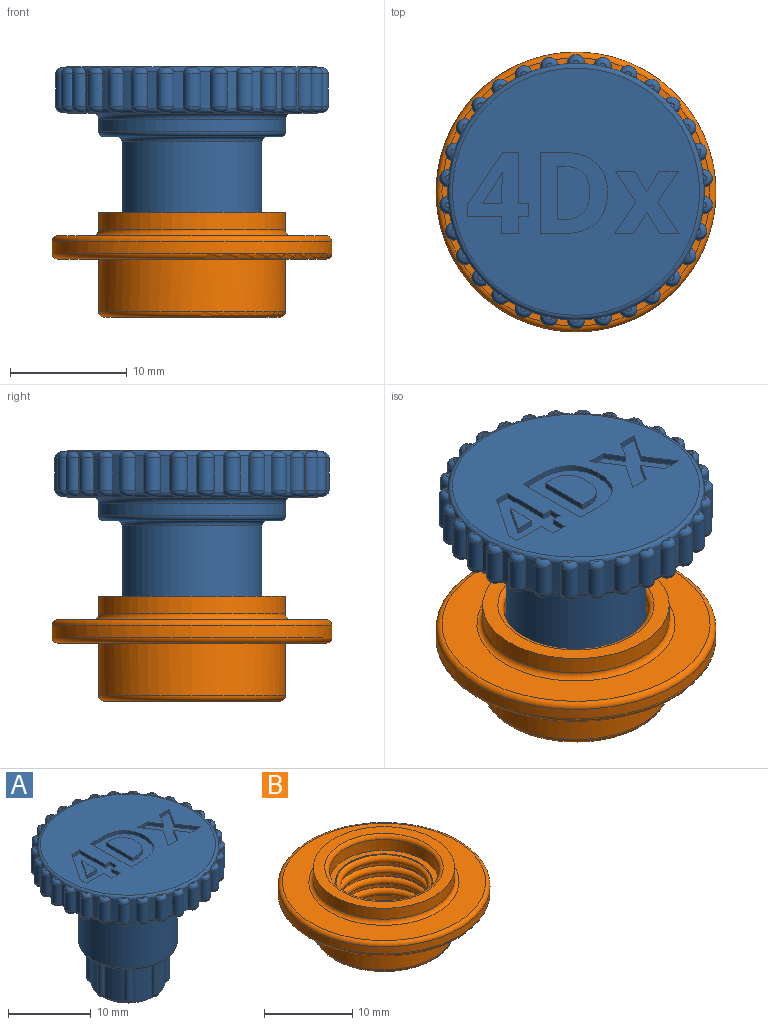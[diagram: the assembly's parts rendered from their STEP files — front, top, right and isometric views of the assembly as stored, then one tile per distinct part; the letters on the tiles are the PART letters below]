
ASSEMBLY  parts=2 mates=1
PART A: 334 faces, bbox 23.8x23.8x20.5 mm
  f0: plane 21.2x21.2mm, normal (0,0,1), area 281.4mm2, adj f53,f291,f292,f293,f294,f295,f296,f297
  f1: cylinder r=4.5mm len=5.3mm, axis (0,0,-1), area 13.7mm2, adj f9,f268,f269,f276,f285,f286
  f2: cylinder r=4.5mm len=5.3mm, axis (0,0,-1), area 13.7mm2, adj f10,f269,f270,f276,f284,f285
  f3: cylinder r=4.5mm len=5.3mm, axis (0,0,-1), area 13.7mm2, adj f11,f270,f271,f276,f283,f284
  f4: cylinder r=4.5mm len=5.3mm, axis (0,0,-1), area 13.7mm2, adj f12,f271,f272,f276,f282,f283
  f5: cylinder r=4.5mm len=5.3mm, axis (0,0,-1), area 13.7mm2, adj f13,f272,f273,f276,f279,f282
  f6: cylinder r=4.5mm len=5.3mm, axis (0,0,-1), area 13.7mm2, adj f14,f273,f274,f276,f279,f281
  f7: cylinder r=4.5mm len=5.3mm, axis (0,0,-1), area 13.7mm2, adj f15,f274,f275,f276,f280,f281
  f8: cylinder r=4.5mm len=5.3mm, axis (0,0,-1), area 13.7mm2, adj f264,f268,f275,f276,f280,f286
  f9: torus R=4.9mm, axis (0,0,1), area 1.8mm2, adj f1,f46,f268,f269
  f10: torus R=4.9mm, axis (0,0,1), area 1.8mm2, adj f2,f46,f269,f270
  f11: torus R=4.9mm, axis (0,0,1), area 1.8mm2, adj f3,f46,f270,f271
  f12: torus R=4.9mm, axis (0,0,1), area 1.8mm2, adj f4,f46,f271,f272
  f13: torus R=4.9mm, axis (0,0,1), area 1.8mm2, adj f5,f46,f272,f273
  f14: torus R=4.9mm, axis (0,0,1), area 1.8mm2, adj f6,f46,f273,f274
  f15: torus R=4.9mm, axis (0,0,1), area 1.8mm2, adj f7,f46,f274,f275
  f16: cylinder r=11mm len=3.2mm, axis (0,0,-1), area 2.6mm2, adj f52,f53,f154,f155,f156,f168,f169,f170
  f17: cylinder r=11mm len=3.2mm, axis (0,0,-1), area 2.6mm2, adj f52,f53,f147,f148,f149,f168,f169,f170
  f18: cylinder r=11mm len=3.2mm, axis (0,0,-1), area 2.6mm2, adj f52,f53,f147,f148,f149,f175,f176,f177
  f19: cylinder r=11mm len=3.2mm, axis (0,0,-1), area 2.6mm2, adj f52,f53,f140,f141,f142,f175,f176,f177
  f20: cylinder r=11mm len=3.2mm, axis (0,0,-1), area 2.6mm2, adj f52,f53,f140,f141,f142,f182,f183,f184
  f21: cylinder r=11mm len=3.2mm, axis (0,0,-1), area 2.6mm2, adj f52,f53,f133,f134,f135,f182,f183,f184
  f22: cylinder r=11mm len=3.2mm, axis (0,0,-1), area 2.6mm2, adj f52,f53,f133,f134,f135,f189,f190,f191
  f23: cylinder r=11mm len=3.2mm, axis (0,0,-1), area 2.6mm2, adj f52,f53,f126,f127,f128,f189,f190,f191
  f24: cylinder r=11mm len=3.2mm, axis (0,0,-1), area 2.6mm2, adj f52,f53,f126,f127,f128,f196,f197,f198
  f25: cylinder r=11mm len=3.2mm, axis (0,0,-1), area 2.6mm2, adj f52,f53,f119,f120,f121,f196,f197,f198
  f26: cylinder r=11mm len=3.2mm, axis (0,0,-1), area 2.6mm2, adj f52,f53,f119,f120,f121,f203,f204,f205
  f27: cylinder r=11mm len=3.2mm, axis (0,0,-1), area 2.6mm2, adj f52,f53,f112,f113,f114,f203,f204,f205
  f28: cylinder r=11mm len=3.2mm, axis (0,0,-1), area 2.6mm2, adj f52,f53,f112,f113,f114,f210,f211,f212
  f29: cylinder r=11mm len=3.2mm, axis (0,0,-1), area 2.6mm2, adj f52,f53,f105,f106,f107,f210,f211,f212
  f30: cylinder r=11mm len=3.2mm, axis (0,0,-1), area 2.6mm2, adj f52,f53,f105,f106,f107,f217,f218,f219
  f31: cylinder r=11mm len=3.2mm, axis (0,0,-1), area 2.6mm2, adj f52,f53,f98,f99,f100,f217,f218,f219
  f32: cylinder r=11mm len=3.2mm, axis (0,0,-1), area 2.6mm2, adj f52,f53,f98,f99,f100,f224,f225,f226
  f33: cylinder r=11mm len=3.2mm, axis (0,0,-1), area 2.6mm2, adj f52,f53,f91,f92,f93,f224,f225,f226
  f34: cylinder r=11mm len=3.2mm, axis (0,0,-1), area 2.6mm2, adj f52,f53,f91,f92,f93,f231,f232,f233
  f35: cylinder r=11mm len=3.2mm, axis (0,0,-1), area 2.6mm2, adj f52,f53,f84,f85,f86,f231,f232,f233
  f36: cylinder r=11mm len=3.2mm, axis (0,0,-1), area 2.6mm2, adj f52,f53,f84,f85,f86,f238,f239,f240
  f37: cylinder r=11mm len=3.2mm, axis (0,0,-1), area 2.6mm2, adj f52,f53,f77,f78,f79,f238,f239,f240
  f38: cylinder r=11mm len=3.2mm, axis (0,0,-1), area 2.6mm2, adj f52,f53,f77,f78,f79,f245,f246,f247
  f39: cylinder r=11mm len=3.2mm, axis (0,0,-1), area 2.6mm2, adj f52,f53,f70,f71,f72,f245,f246,f247
  f40: cylinder r=11mm len=3.2mm, axis (0,0,-1), area 2.6mm2, adj f52,f53,f70,f71,f72,f252,f253,f254
  f41: cylinder r=11mm len=3.2mm, axis (0,0,-1), area 2.6mm2, adj f52,f53,f63,f64,f65,f252,f253,f254
  f42: cylinder r=11mm len=3.2mm, axis (0,0,-1), area 2.6mm2, adj f52,f53,f63,f64,f65,f259,f262,f263
  f43: cylinder r=11mm len=3.2mm, axis (0,0,-1), area 2.6mm2, adj f52,f53,f56,f59,f60,f259,f262,f263
  f44: cylinder r=11mm len=3.2mm, axis (0,0,-1), area 2.6mm2, adj f52,f53,f56,f59,f60,f161,f162,f163
  f45: cylinder r=11mm len=3.2mm, axis (0,0,-1), area 2.6mm2, adj f52,f53,f154,f155,f156,f161,f162,f163
  f46: plane 11.2x11.2mm, normal (0,0,-1), area 22.7mm2, adj f9,f10,f11,f12,f13,f14,f15,f264
  f47: cylinder r=6mm len=12mm, axis (0,0,-1), area 290.3mm2, adj f265,f266
  f48: plane 15.2x15.2mm, normal (0,0,-1), area 52.8mm2, adj f266,f267
  f49: cylinder r=8mm len=16mm, axis (0,0,-1), area 55.3mm2, adj f51,f267
  f50: plane 21.2x21.2mm, normal (0,0,-1), area 126mm2, adj f51,f52
  f51: torus R=8.5mm, axis (0,0,1), area 40.4mm2, adj f49,f50
  f52: torus R=10.6mm, axis (0,0,1), area 42.9mm2, adj f16,f17,f18,f19,f20,f21,f22,f23
  f53: torus R=10.6mm, axis (0,0,-1), area 42.9mm2, adj f0,f16,f17,f18,f19,f20,f21,f22
  f54: cylinder r=11mm len=1.42mm, axis (0,0,1), area 0.3mm2, adj f52,f57,f60
  f55: cylinder r=11mm len=1.42mm, axis (0,0,1), area 0.3mm2, adj f53,f58,f59
  f56: cylinder r=0.75mm len=2.81mm, axis (0,0,1), area 6.8mm2, adj f43,f44,f59,f60
  f57: plane 0.5x0.25mm, normal (0,0,-1), area 0.1mm2, adj f54,f60
  f58: plane 0.5x0.25mm, normal (0,0,1), area 0.1mm2, adj f55,f59
  f59: torus R=0.25mm, axis (0,0,1), area 1.4mm2, adj f43,f44,f55,f56,f58
  f60: torus R=0.25mm, axis (0,0,1), area 1.4mm2, adj f43,f44,f54,f56,f57
  f61: plane 0.48x0.35mm, normal (0,0,1), area 0.1mm2, adj f65,f66
  f62: plane 0.48x0.35mm, normal (0,0,-1), area 0.1mm2, adj f64,f67
  f63: cylinder r=0.75mm len=2.81mm, axis (0,0,1), area 6.8mm2, adj f41,f42,f64,f65
  f64: torus R=0.25mm, axis (0,0,1), area 1.4mm2, adj f41,f42,f62,f63,f67
  f65: torus R=0.25mm, axis (0,0,1), area 1.4mm2, adj f41,f42,f61,f63,f66
  f66: cylinder r=11mm len=1.29mm, axis (0,0,1), area 0.3mm2, adj f53,f61,f65
  f67: cylinder r=11mm len=1.3mm, axis (0,0,1), area 0.3mm2, adj f52,f62,f64
  f68: plane 0.44x0.42mm, normal (0,0,1), area 0.1mm2, adj f72,f73
  f69: plane 0.44x0.42mm, normal (0,0,-1), area 0.1mm2, adj f71,f74
  f70: cylinder r=0.75mm len=2.81mm, axis (0,0,1), area 6.8mm2, adj f39,f40,f71,f72
  f71: torus R=0.25mm, axis (0,0,1), area 1.4mm2, adj f39,f40,f69,f70,f74
  f72: torus R=0.25mm, axis (0,0,1), area 1.4mm2, adj f39,f40,f68,f70,f73
  f73: cylinder r=11mm len=1.05mm, axis (0,0,1), area 0.3mm2, adj f53,f68,f72
  f74: cylinder r=11mm len=1.06mm, axis (0,0,1), area 0.3mm2, adj f52,f69,f71
  f75: plane 0.49x0.33mm, normal (0,0,1), area 0.1mm2, adj f79,f80
  f76: plane 0.49x0.33mm, normal (0,0,-1), area 0.1mm2, adj f78,f81
  f77: cylinder r=0.75mm len=2.81mm, axis (0,0,1), area 6.8mm2, adj f37,f38,f78,f79
  f78: torus R=0.25mm, axis (0,0,1), area 1.4mm2, adj f37,f38,f76,f77,f81
  f79: torus R=0.25mm, axis (0,0,1), area 1.4mm2, adj f37,f38,f75,f77,f80
  f80: cylinder r=11mm len=1.35mm, axis (0,0,1), area 0.3mm2, adj f53,f75,f79
  f81: cylinder r=11mm len=1.35mm, axis (0,0,1), area 0.3mm2, adj f52,f76,f78
  f82: plane 0.5x0.28mm, normal (0,0,1), area 0.1mm2, adj f86,f87
  f83: plane 0.5x0.28mm, normal (0,0,-1), area 0.1mm2, adj f85,f88
  f84: cylinder r=0.75mm len=2.81mm, axis (0,0,1), area 6.8mm2, adj f35,f36,f85,f86
  f85: torus R=0.25mm, axis (0,0,1), area 1.4mm2, adj f35,f36,f83,f84,f88
  f86: torus R=0.25mm, axis (0,0,1), area 1.4mm2, adj f35,f36,f82,f84,f87
  f87: cylinder r=11mm len=1.41mm, axis (0,0,1), area 0.3mm2, adj f53,f82,f86
  f88: cylinder r=11mm len=1.42mm, axis (0,0,1), area 0.3mm2, adj f52,f83,f85
  f89: plane 0.47x0.38mm, normal (0,0,1), area 0.1mm2, adj f93,f94
  f90: plane 0.47x0.38mm, normal (0,0,-1), area 0.1mm2, adj f92,f95
  f91: cylinder r=0.75mm len=2.81mm, axis (0,0,1), area 6.8mm2, adj f33,f34,f92,f93
  f92: torus R=0.25mm, axis (0,0,1), area 1.4mm2, adj f33,f34,f90,f91,f95
  f93: torus R=0.25mm, axis (0,0,1), area 1.4mm2, adj f33,f34,f89,f91,f94
  f94: cylinder r=11mm len=1.23mm, axis (0,0,1), area 0.3mm2, adj f53,f89,f93
  f95: cylinder r=11mm len=1.23mm, axis (0,0,1), area 0.3mm2, adj f52,f90,f92
  f96: plane 0.45x0.4mm, normal (0,0,1), area 0.1mm2, adj f100,f101
  f97: plane 0.45x0.4mm, normal (0,0,-1), area 0.1mm2, adj f99,f102
  f98: cylinder r=0.75mm len=2.81mm, axis (0,0,1), area 6.8mm2, adj f31,f32,f99,f100
  f99: torus R=0.25mm, axis (0,0,1), area 1.4mm2, adj f31,f32,f97,f98,f102
  f100: torus R=0.25mm, axis (0,0,1), area 1.4mm2, adj f31,f32,f96,f98,f101
  f101: cylinder r=11mm len=1.15mm, axis (0,0,1), area 0.3mm2, adj f53,f96,f100
  f102: cylinder r=11mm len=1.15mm, axis (0,0,1), area 0.3mm2, adj f52,f97,f99
  f103: plane 0.5x0.3mm, normal (0,0,1), area 0.1mm2, adj f107,f108
  f104: plane 0.5x0.3mm, normal (0,0,-1), area 0.1mm2, adj f106,f109
  f105: cylinder r=0.75mm len=2.81mm, axis (0,0,1), area 6.8mm2, adj f29,f30,f106,f107
  f106: torus R=0.25mm, axis (0,0,1), area 1.4mm2, adj f29,f30,f104,f105,f109
  f107: torus R=0.25mm, axis (0,0,1), area 1.4mm2, adj f29,f30,f103,f105,f108
  f108: cylinder r=11mm len=1.39mm, axis (0,0,1), area 0.3mm2, adj f53,f103,f107
  f109: cylinder r=11mm len=1.39mm, axis (0,0,1), area 0.3mm2, adj f52,f104,f106
  f110: plane 0.5x0.3mm, normal (0,0,1), area 0.1mm2, adj f114,f115
  f111: plane 0.5x0.3mm, normal (0,0,-1), area 0.1mm2, adj f113,f116
  f112: cylinder r=0.75mm len=2.81mm, axis (0,0,1), area 6.8mm2, adj f27,f28,f113,f114
  f113: torus R=0.25mm, axis (0,0,1), area 1.4mm2, adj f27,f28,f111,f112,f116
  f114: torus R=0.25mm, axis (0,0,1), area 1.4mm2, adj f27,f28,f110,f112,f115
  f115: cylinder r=11mm len=1.39mm, axis (0,0,1), area 0.3mm2, adj f53,f110,f114
  f116: cylinder r=11mm len=1.39mm, axis (0,0,1), area 0.3mm2, adj f52,f111,f113
  f117: plane 0.45x0.4mm, normal (0,0,1), area 0.1mm2, adj f121,f122
  f118: plane 0.45x0.4mm, normal (0,0,-1), area 0.1mm2, adj f120,f123
  f119: cylinder r=0.75mm len=2.81mm, axis (0,0,1), area 6.8mm2, adj f25,f26,f120,f121
  f120: torus R=0.25mm, axis (0,0,1), area 1.4mm2, adj f25,f26,f118,f119,f123
  f121: torus R=0.25mm, axis (0,0,1), area 1.4mm2, adj f25,f26,f117,f119,f122
  f122: cylinder r=11mm len=1.15mm, axis (0,0,1), area 0.3mm2, adj f53,f117,f121
  f123: cylinder r=11mm len=1.15mm, axis (0,0,1), area 0.3mm2, adj f52,f118,f120
  f124: plane 0.47x0.38mm, normal (0,0,1), area 0.1mm2, adj f128,f129
  f125: plane 0.47x0.38mm, normal (0,0,-1), area 0.1mm2, adj f127,f130
  f126: cylinder r=0.75mm len=2.81mm, axis (0,0,1), area 6.8mm2, adj f23,f24,f127,f128
  f127: torus R=0.25mm, axis (0,0,1), area 1.4mm2, adj f23,f24,f125,f126,f130
  f128: torus R=0.25mm, axis (0,0,1), area 1.4mm2, adj f23,f24,f124,f126,f129
  f129: cylinder r=11mm len=1.23mm, axis (0,0,1), area 0.3mm2, adj f53,f124,f128
  f130: cylinder r=11mm len=1.23mm, axis (0,0,1), area 0.3mm2, adj f52,f125,f127
  f131: plane 0.5x0.28mm, normal (0,0,1), area 0.1mm2, adj f135,f136
  f132: plane 0.5x0.28mm, normal (0,0,-1), area 0.1mm2, adj f134,f137
  f133: cylinder r=0.75mm len=2.81mm, axis (0,0,1), area 6.8mm2, adj f21,f22,f134,f135
  f134: torus R=0.25mm, axis (0,0,1), area 1.4mm2, adj f21,f22,f132,f133,f137
  f135: torus R=0.25mm, axis (0,0,1), area 1.4mm2, adj f21,f22,f131,f133,f136
  f136: cylinder r=11mm len=1.41mm, axis (0,0,1), area 0.3mm2, adj f53,f131,f135
  f137: cylinder r=11mm len=1.42mm, axis (0,0,1), area 0.3mm2, adj f52,f132,f134
  f138: plane 0.49x0.33mm, normal (0,0,1), area 0.1mm2, adj f142,f143
  f139: plane 0.49x0.33mm, normal (0,0,-1), area 0.1mm2, adj f141,f144
  f140: cylinder r=0.75mm len=2.81mm, axis (0,0,1), area 6.8mm2, adj f19,f20,f141,f142
  f141: torus R=0.25mm, axis (0,0,1), area 1.4mm2, adj f19,f20,f139,f140,f144
  f142: torus R=0.25mm, axis (0,0,1), area 1.4mm2, adj f19,f20,f138,f140,f143
  f143: cylinder r=11mm len=1.35mm, axis (0,0,1), area 0.3mm2, adj f53,f138,f142
  f144: cylinder r=11mm len=1.35mm, axis (0,0,1), area 0.3mm2, adj f52,f139,f141
  f145: plane 0.44x0.42mm, normal (0,0,1), area 0.1mm2, adj f149,f150
  f146: plane 0.44x0.42mm, normal (0,0,-1), area 0.1mm2, adj f148,f151
  f147: cylinder r=0.75mm len=2.81mm, axis (0,0,1), area 6.8mm2, adj f17,f18,f148,f149
  f148: torus R=0.25mm, axis (0,0,1), area 1.4mm2, adj f17,f18,f146,f147,f151
  f149: torus R=0.25mm, axis (0,0,1), area 1.4mm2, adj f17,f18,f145,f147,f150
  f150: cylinder r=11mm len=1.05mm, axis (0,0,1), area 0.3mm2, adj f53,f145,f149
  f151: cylinder r=11mm len=1.06mm, axis (0,0,1), area 0.3mm2, adj f52,f146,f148
  f152: plane 0.48x0.35mm, normal (0,0,-1), area 0.1mm2, adj f156,f158
  f153: plane 0.48x0.35mm, normal (0,0,1), area 0.1mm2, adj f155,f157
  f154: cylinder r=0.75mm len=2.81mm, axis (0,0,1), area 6.8mm2, adj f16,f45,f155,f156
  f155: torus R=0.25mm, axis (0,0,1), area 1.4mm2, adj f16,f45,f153,f154,f157
  f156: torus R=0.25mm, axis (0,0,1), area 1.4mm2, adj f16,f45,f152,f154,f158
  f157: cylinder r=11mm len=1.29mm, axis (0,0,1), area 0.3mm2, adj f53,f153,f155
  f158: cylinder r=11mm len=1.3mm, axis (0,0,1), area 0.3mm2, adj f52,f152,f156
  f159: plane 0.5x0.3mm, normal (0,0,1), area 0.1mm2, adj f163,f165
  f160: plane 0.5x0.3mm, normal (0,0,-1), area 0.1mm2, adj f162,f164
  f161: cylinder r=0.75mm len=2.81mm, axis (0,0,1), area 6.8mm2, adj f44,f45,f162,f163
  f162: torus R=0.25mm, axis (0,0,1), area 1.4mm2, adj f44,f45,f160,f161,f164
  f163: torus R=0.25mm, axis (0,0,1), area 1.4mm2, adj f44,f45,f159,f161,f165
  f164: cylinder r=11mm len=1.39mm, axis (0,0,1), area 0.3mm2, adj f52,f160,f162
  f165: cylinder r=11mm len=1.39mm, axis (0,0,1), area 0.3mm2, adj f53,f159,f163
  f166: plane 0.45x0.4mm, normal (0,0,1), area 0.1mm2, adj f170,f172
  f167: plane 0.45x0.4mm, normal (0,0,-1), area 0.1mm2, adj f169,f171
  f168: cylinder r=0.75mm len=2.81mm, axis (0,0,1), area 6.8mm2, adj f16,f17,f169,f170
  f169: torus R=0.25mm, axis (0,0,1), area 1.4mm2, adj f16,f17,f167,f168,f171
  f170: torus R=0.25mm, axis (0,0,1), area 1.4mm2, adj f16,f17,f166,f168,f172
  f171: cylinder r=11mm len=1.15mm, axis (0,0,1), area 0.3mm2, adj f52,f167,f169
  f172: cylinder r=11mm len=1.15mm, axis (0,0,1), area 0.3mm2, adj f53,f166,f170
  f173: plane 0.47x0.38mm, normal (0,0,1), area 0.1mm2, adj f177,f179
  f174: plane 0.47x0.38mm, normal (0,0,-1), area 0.1mm2, adj f176,f178
  f175: cylinder r=0.75mm len=2.81mm, axis (0,0,1), area 6.8mm2, adj f18,f19,f176,f177
  f176: torus R=0.25mm, axis (0,0,1), area 1.4mm2, adj f18,f19,f174,f175,f178
  f177: torus R=0.25mm, axis (0,0,1), area 1.4mm2, adj f18,f19,f173,f175,f179
  f178: cylinder r=11mm len=1.23mm, axis (0,0,1), area 0.3mm2, adj f52,f174,f176
  f179: cylinder r=11mm len=1.23mm, axis (0,0,1), area 0.3mm2, adj f53,f173,f177
  f180: plane 0.5x0.28mm, normal (0,0,1), area 0.1mm2, adj f184,f186
  f181: plane 0.5x0.28mm, normal (0,0,-1), area 0.1mm2, adj f183,f185
  f182: cylinder r=0.75mm len=2.81mm, axis (0,0,1), area 6.8mm2, adj f20,f21,f183,f184
  f183: torus R=0.25mm, axis (0,0,1), area 1.4mm2, adj f20,f21,f181,f182,f185
  f184: torus R=0.25mm, axis (0,0,1), area 1.4mm2, adj f20,f21,f180,f182,f186
  f185: cylinder r=11mm len=1.42mm, axis (0,0,1), area 0.3mm2, adj f52,f181,f183
  f186: cylinder r=11mm len=1.41mm, axis (0,0,1), area 0.3mm2, adj f53,f180,f184
  f187: plane 0.49x0.33mm, normal (0,0,1), area 0.1mm2, adj f191,f193
  f188: plane 0.49x0.33mm, normal (0,0,-1), area 0.1mm2, adj f190,f192
  f189: cylinder r=0.75mm len=2.81mm, axis (0,0,1), area 6.8mm2, adj f22,f23,f190,f191
  f190: torus R=0.25mm, axis (0,0,1), area 1.4mm2, adj f22,f23,f188,f189,f192
  f191: torus R=0.25mm, axis (0,0,1), area 1.4mm2, adj f22,f23,f187,f189,f193
  f192: cylinder r=11mm len=1.35mm, axis (0,0,1), area 0.3mm2, adj f52,f188,f190
  f193: cylinder r=11mm len=1.35mm, axis (0,0,1), area 0.3mm2, adj f53,f187,f191
  f194: plane 0.44x0.42mm, normal (0,0,1), area 0.1mm2, adj f198,f200
  f195: plane 0.44x0.42mm, normal (0,0,-1), area 0.1mm2, adj f197,f199
  f196: cylinder r=0.75mm len=2.81mm, axis (0,0,1), area 6.8mm2, adj f24,f25,f197,f198
  f197: torus R=0.25mm, axis (0,0,1), area 1.4mm2, adj f24,f25,f195,f196,f199
  f198: torus R=0.25mm, axis (0,0,1), area 1.4mm2, adj f24,f25,f194,f196,f200
  f199: cylinder r=11mm len=1.06mm, axis (0,0,1), area 0.3mm2, adj f52,f195,f197
  f200: cylinder r=11mm len=1.05mm, axis (0,0,1), area 0.3mm2, adj f53,f194,f198
  f201: plane 0.48x0.35mm, normal (0,0,1), area 0.1mm2, adj f205,f207
  f202: plane 0.48x0.35mm, normal (0,0,-1), area 0.1mm2, adj f204,f206
  f203: cylinder r=0.75mm len=2.81mm, axis (0,0,1), area 6.8mm2, adj f26,f27,f204,f205
  f204: torus R=0.25mm, axis (0,0,1), area 1.4mm2, adj f26,f27,f202,f203,f206
  f205: torus R=0.25mm, axis (0,0,1), area 1.4mm2, adj f26,f27,f201,f203,f207
  f206: cylinder r=11mm len=1.3mm, axis (0,0,1), area 0.3mm2, adj f52,f202,f204
  f207: cylinder r=11mm len=1.29mm, axis (0,0,1), area 0.3mm2, adj f53,f201,f205
  f208: plane 0.5x0.25mm, normal (0,0,1), area 0.1mm2, adj f212,f214
  f209: plane 0.5x0.25mm, normal (0,0,-1), area 0.1mm2, adj f211,f213
  f210: cylinder r=0.75mm len=2.81mm, axis (0,0,1), area 6.8mm2, adj f28,f29,f211,f212
  f211: torus R=0.25mm, axis (0,0,1), area 1.4mm2, adj f28,f29,f209,f210,f213
  f212: torus R=0.25mm, axis (0,0,1), area 1.4mm2, adj f28,f29,f208,f210,f214
  f213: cylinder r=11mm len=1.42mm, axis (0,0,1), area 0.3mm2, adj f52,f209,f211
  f214: cylinder r=11mm len=1.42mm, axis (0,0,1), area 0.3mm2, adj f53,f208,f212
  f215: plane 0.48x0.35mm, normal (0,0,1), area 0.1mm2, adj f219,f221
  f216: plane 0.48x0.35mm, normal (0,0,-1), area 0.1mm2, adj f218,f220
  f217: cylinder r=0.75mm len=2.81mm, axis (0,0,1), area 6.8mm2, adj f30,f31,f218,f219
  f218: torus R=0.25mm, axis (0,0,1), area 1.4mm2, adj f30,f31,f216,f217,f220
  f219: torus R=0.25mm, axis (0,0,1), area 1.4mm2, adj f30,f31,f215,f217,f221
  f220: cylinder r=11mm len=1.3mm, axis (0,0,1), area 0.3mm2, adj f52,f216,f218
  f221: cylinder r=11mm len=1.29mm, axis (0,0,1), area 0.3mm2, adj f53,f215,f219
  f222: plane 0.44x0.42mm, normal (0,0,1), area 0.1mm2, adj f226,f228
  f223: plane 0.44x0.42mm, normal (0,0,-1), area 0.1mm2, adj f225,f227
  f224: cylinder r=0.75mm len=2.81mm, axis (0,0,1), area 6.8mm2, adj f32,f33,f225,f226
  f225: torus R=0.25mm, axis (0,0,1), area 1.4mm2, adj f32,f33,f223,f224,f227
  f226: torus R=0.25mm, axis (0,0,1), area 1.4mm2, adj f32,f33,f222,f224,f228
  f227: cylinder r=11mm len=1.06mm, axis (0,0,1), area 0.3mm2, adj f52,f223,f225
  f228: cylinder r=11mm len=1.05mm, axis (0,0,1), area 0.3mm2, adj f53,f222,f226
  f229: plane 0.49x0.33mm, normal (0,0,1), area 0.1mm2, adj f233,f235
  f230: plane 0.49x0.33mm, normal (0,0,-1), area 0.1mm2, adj f232,f234
  f231: cylinder r=0.75mm len=2.81mm, axis (0,0,1), area 6.8mm2, adj f34,f35,f232,f233
  f232: torus R=0.25mm, axis (0,0,1), area 1.4mm2, adj f34,f35,f230,f231,f234
  f233: torus R=0.25mm, axis (0,0,1), area 1.4mm2, adj f34,f35,f229,f231,f235
  f234: cylinder r=11mm len=1.35mm, axis (0,0,1), area 0.3mm2, adj f52,f230,f232
  f235: cylinder r=11mm len=1.35mm, axis (0,0,1), area 0.3mm2, adj f53,f229,f233
  f236: plane 0.5x0.28mm, normal (0,0,1), area 0.1mm2, adj f240,f242
  f237: plane 0.5x0.28mm, normal (0,0,-1), area 0.1mm2, adj f239,f241
  f238: cylinder r=0.75mm len=2.81mm, axis (0,0,1), area 6.8mm2, adj f36,f37,f239,f240
  f239: torus R=0.25mm, axis (0,0,1), area 1.4mm2, adj f36,f37,f237,f238,f241
  f240: torus R=0.25mm, axis (0,0,1), area 1.4mm2, adj f36,f37,f236,f238,f242
  f241: cylinder r=11mm len=1.42mm, axis (0,0,1), area 0.3mm2, adj f52,f237,f239
  f242: cylinder r=11mm len=1.41mm, axis (0,0,1), area 0.3mm2, adj f53,f236,f240
  f243: plane 0.47x0.38mm, normal (0,0,1), area 0.1mm2, adj f247,f249
  f244: plane 0.47x0.38mm, normal (0,0,-1), area 0.1mm2, adj f246,f248
  f245: cylinder r=0.75mm len=2.81mm, axis (0,0,1), area 6.8mm2, adj f38,f39,f246,f247
  f246: torus R=0.25mm, axis (0,0,1), area 1.4mm2, adj f38,f39,f244,f245,f248
  f247: torus R=0.25mm, axis (0,0,1), area 1.4mm2, adj f38,f39,f243,f245,f249
  f248: cylinder r=11mm len=1.23mm, axis (0,0,1), area 0.3mm2, adj f52,f244,f246
  f249: cylinder r=11mm len=1.23mm, axis (0,0,1), area 0.3mm2, adj f53,f243,f247
  f250: plane 0.45x0.4mm, normal (0,0,1), area 0.1mm2, adj f254,f256
  f251: plane 0.45x0.4mm, normal (0,0,-1), area 0.1mm2, adj f253,f255
  f252: cylinder r=0.75mm len=2.81mm, axis (0,0,1), area 6.8mm2, adj f40,f41,f253,f254
  f253: torus R=0.25mm, axis (0,0,1), area 1.4mm2, adj f40,f41,f251,f252,f255
  f254: torus R=0.25mm, axis (0,0,1), area 1.4mm2, adj f40,f41,f250,f252,f256
  f255: cylinder r=11mm len=1.15mm, axis (0,0,1), area 0.3mm2, adj f52,f251,f253
  f256: cylinder r=11mm len=1.15mm, axis (0,0,1), area 0.3mm2, adj f53,f250,f254
  f257: cylinder r=11mm len=1.39mm, axis (0,0,1), area 0.3mm2, adj f52,f260,f263
  f258: cylinder r=11mm len=1.39mm, axis (0,0,1), area 0.3mm2, adj f53,f261,f262
  f259: cylinder r=0.75mm len=2.81mm, axis (0,0,1), area 6.8mm2, adj f42,f43,f262,f263
  f260: plane 0.5x0.3mm, normal (0,0,-1), area 0.1mm2, adj f257,f263
  f261: plane 0.5x0.3mm, normal (0,0,1), area 0.1mm2, adj f258,f262
  f262: torus R=0.25mm, axis (0,0,1), area 1.4mm2, adj f42,f43,f258,f259,f261
  f263: torus R=0.25mm, axis (0,0,1), area 1.4mm2, adj f42,f43,f257,f259,f260
  f264: torus R=4.9mm, axis (0,0,1), area 1.8mm2, adj f8,f46,f268,f275
  f265: torus R=5.6mm, axis (0,0,1), area 23.1mm2, adj f46,f47
  f266: torus R=6.4mm, axis (0,0,1), area 24.3mm2, adj f47,f48
  f267: torus R=7.6mm, axis (0,0,1), area 31mm2, adj f48,f49
  f268: cylinder r=0.5mm len=5.2mm, axis (0,0,-1), area 8.3mm2, adj f1,f8,f9,f46,f264,f286
  f269: cylinder r=0.5mm len=5.2mm, axis (0,0,-1), area 8.3mm2, adj f1,f2,f9,f10,f46,f285
  f270: cylinder r=0.5mm len=5.2mm, axis (0,0,-1), area 8.3mm2, adj f2,f3,f10,f11,f46,f284
  f271: cylinder r=0.5mm len=5.2mm, axis (0,0,-1), area 8.3mm2, adj f3,f4,f11,f12,f46,f283
  f272: cylinder r=0.5mm len=5.2mm, axis (0,0,-1), area 8.3mm2, adj f4,f5,f12,f13,f46,f282
  f273: cylinder r=0.5mm len=5.2mm, axis (0,0,-1), area 8.3mm2, adj f5,f6,f13,f14,f46,f279
  f274: cylinder r=0.5mm len=5.2mm, axis (0,0,-1), area 8.3mm2, adj f6,f7,f14,f15,f46,f281
  f275: cylinder r=0.5mm len=5.2mm, axis (0,0,-1), area 8.3mm2, adj f7,f8,f15,f46,f264,f280
  f276: plane 9x9mm, normal (0,0,-1), area 0.4mm2, adj f1,f2,f3,f4,f5,f6,f7,f8
  f277: plane 8.2x8.2mm, normal (0,0,-1), area 52.8mm2, adj f278
  f278: torus R=4.1mm, axis (0,0,1), area 14.3mm2, adj f276,f277
  f279: sphere r=0.5mm, area 0.8mm2, adj f5,f6,f273
  f280: sphere r=0.5mm, area 0.7mm2, adj f7,f8,f275
  f281: sphere r=0.5mm, area 0.8mm2, adj f6,f7,f274
  f282: sphere r=0.5mm, area 0.8mm2, adj f4,f5,f272
  f283: sphere r=0.5mm, area 0.8mm2, adj f3,f4,f271
  f284: sphere r=0.5mm, area 0.8mm2, adj f2,f3,f270
  f285: sphere r=0.5mm, area 0.8mm2, adj f1,f2,f269
  f286: sphere r=0.5mm, area 0.8mm2, adj f1,f8,f268
  f287: extruded ~2.24x1.98mm, area 1.7mm2, adj f288,f298,f299,f332
  f288: extruded ~2.28x2.13mm, area 1.8mm2, adj f287,f289,f299,f332
  f289: plane 0.63x0.5mm, normal (0,-1,0), area 0.3mm2, adj f288,f290,f299,f332
  f290: plane 4.52x0.5mm, normal (-1,0,0), area 2.3mm2, adj f289,f298,f299,f332
  f291: extruded ~2.63x0.98mm, area 1.4mm2, adj f0,f292,f297,f299
  f292: extruded ~2.51x0.94mm, area 1.4mm2, adj f0,f291,f293,f299
  f293: extruded ~2.64x0.9mm, area 1.4mm2, adj f0,f292,f294,f299
  f294: plane 2.18x0.5mm, normal (0,-1,0), area 1.1mm2, adj f0,f293,f295,f299
  f295: plane 6.94x0.5mm, normal (1,0,0), area 3.5mm2, adj f0,f294,f296,f299
  f296: plane 1.97x0.5mm, normal (0,1,0), area 1mm2, adj f0,f295,f297,f299
  f297: extruded ~2.82x0.91mm, area 1.5mm2, adj f0,f291,f296,f299
  f298: plane 0.78x0.5mm, normal (0,1,0), area 0.4mm2, adj f287,f290,f299,f332
  f299: plane 6.94x5.76mm, normal (0,0,1), area 24.5mm2, adj f287,f288,f289,f290,f291,f292,f293,f294
  f300: plane 1.18x0.5mm, normal (1,0,0), area 0.6mm2, adj f301,f317,f318,f333
  f301: plane 1.67x0.5mm, normal (0,-1,0), area 0.8mm2, adj f300,f302,f318,f333
  f302: plane 1.92x1.27mm, normal (-0.83,0.55,0), area 1.2mm2, adj f301,f303,f318,f333
  f303: extruded ~0.76x0.5mm, area 0.4mm2, adj f302,f304,f318,f333
  f304: plane 0.5x0.04mm, normal (0,1,0), area 0mm2, adj f303,f305,f318,f333
  f305: extruded ~0.65x0.5mm, area 0.3mm2, adj f304,f317,f318,f333
  f306: plane 0.84x0.5mm, normal (0,1,0), area 0.4mm2, adj f0,f307,f316,f318
  f307: plane 1.14x0.5mm, normal (-1,0,0), area 0.6mm2, adj f0,f306,f308,f318
  f308: plane 0.84x0.5mm, normal (0,-1,0), area 0.4mm2, adj f0,f307,f309,f318
  f309: plane 4.36x0.5mm, normal (-1,0,0), area 2.2mm2, adj f0,f308,f310,f318
  f310: plane 1.35x0.5mm, normal (0,-1,0), area 0.7mm2, adj f0,f309,f311,f318
  f311: plane 4.48x3.04mm, normal (0.83,-0.56,0), area 2.7mm2, adj f0,f310,f312,f318
  f312: plane 1.02x0.5mm, normal (1,0,0), area 0.5mm2, adj f0,f311,f313,f318
  f313: plane 2.96x0.5mm, normal (0,1,0), area 1.5mm2, adj f0,f312,f314,f318
  f314: plane 1.44x0.5mm, normal (1,0,0), area 0.7mm2, adj f0,f313,f315,f318
  f315: plane 1.43x0.5mm, normal (0,1,0), area 0.7mm2, adj f0,f314,f316,f318
  f316: plane 1.44x0.5mm, normal (-1,0,0), area 0.7mm2, adj f0,f306,f315,f318
  f317: extruded ~0.85x0.5mm, area 0.4mm2, adj f300,f305,f318,f333
  f318: plane 6.94x5.23mm, normal (0,0,1), area 18.2mm2, adj f300,f301,f302,f303,f304,f305,f306,f307
  f319: plane 2.6x1.71mm, normal (0.84,0.55,0), area 1.6mm2, adj f0,f320,f330,f331
  f320: plane 2.71x1.8mm, normal (0.83,-0.55,0), area 1.6mm2, adj f0,f319,f321,f331
  f321: plane 1.64x0.5mm, normal (0,1,0), area 0.8mm2, adj f0,f320,f322,f331
  f322: plane 1.82x1.12mm, normal (-0.85,0.52,0), area 1.1mm2, adj f0,f321,f323,f331
  f323: plane 1.82x1.12mm, normal (0.85,0.52,0), area 1.1mm2, adj f0,f322,f324,f331
  f324: plane 1.65x0.5mm, normal (0,1,0), area 0.8mm2, adj f0,f323,f325,f331
  f325: plane 2.71x1.81mm, normal (-0.83,-0.56,0), area 1.6mm2, adj f0,f324,f326,f331
  f326: plane 2.6x1.73mm, normal (-0.83,0.55,0), area 1.6mm2, adj f0,f325,f327,f331
  f327: plane 1.64x0.5mm, normal (0,-1,0), area 0.8mm2, adj f0,f326,f328,f331
  f328: plane 1.69x1.04mm, normal (0.85,-0.52,0), area 1mm2, adj f0,f327,f329,f331
  f329: plane 1.69x1.03mm, normal (-0.85,-0.52,0), area 1mm2, adj f0,f328,f330,f331
  f330: plane 1.64x0.5mm, normal (0,-1,0), area 0.8mm2, adj f0,f319,f329,f331
  f331: plane 5.53x5.31mm, normal (0,0,1), area 15.8mm2, adj f319,f320,f321,f322,f323,f324,f325,f326
  f332: plane 4.52x2.76mm, normal (0,0,1), area 10.9mm2, adj f287,f288,f289,f290,f298
  f333: plane 2.68x1.73mm, normal (0,0,1), area 2.2mm2, adj f300,f301,f302,f303,f304,f305,f317
PART B: 26 faces, bbox 26x26x9 mm
  f0: cylinder r=5.5mm len=11mm, axis (0,0,-1), area 33.3mm2, adj f11,f17
  f1: cylinder r=5.5mm len=11mm, axis (0,0,-1), area 1.3mm2, adj f10,f18
  f2: plane 15x15mm, normal (0,0,-1), area 63.6mm2, adj f11,f12
  f3: cylinder r=8mm len=16mm, axis (0,0,-1), area 226.2mm2, adj f4,f12
  f4: plane 23x23mm, normal (0,0,-1), area 214.4mm2, adj f3,f13
  f5: cylinder r=12mm len=24mm, axis (0,0,-1), area 75.4mm2, adj f13,f14
  f6: plane 23x23mm, normal (0,0,1), area 188.5mm2, adj f14,f15
  f7: cylinder r=8mm len=16mm, axis (0,0,-1), area 75.4mm2, adj f8,f15
  f8: plane 16x16mm, normal (0,0,1), area 60mm2, adj f7,f16
  f9: cylinder r=6.2mm len=12.4mm, axis (0,0,-1), area 58.4mm2, adj f10,f16
  f10: plane 12.4x12.4mm, normal (0,0,1), area 25.7mm2, adj f1,f9
  f11: torus R=6mm, axis (0,0,1), area 28mm2, adj f0,f2
  f12: torus R=7.5mm, axis (0,0,1), area 38.6mm2, adj f2,f3
  f13: torus R=11.5mm, axis (0,0,1), area 58.3mm2, adj f4,f5
  f14: torus R=11.5mm, axis (0,0,-1), area 58.3mm2, adj f5,f6
  f15: torus R=8.5mm, axis (0,0,-1), area 40.4mm2, adj f6,f7
  f16: torus R=6.7mm, axis (0,0,-1), area 31.5mm2, adj f8,f9
  f17: plane 11x11mm, normal (0,0,-1), area 3.5mm2, adj f0,f22
  f18: plane 11x11mm, normal (0,0,1), area 3.5mm2, adj f1,f23
  f19: cylinder r=5.4mm len=10.79mm, axis (0,0,1), area 17mm2, adj f20,f25
  f20: torus R=5.4mm, axis (0,0,1), area 50.1mm2, adj f19,f21
  f21: cylinder r=5.4mm len=10.79mm, axis (0,0,1), area 17mm2, adj f20,f22
  f22: torus R=5.4mm, axis (0,0,1), area 50.1mm2, adj f17,f21
  f23: torus R=5.4mm, axis (0,0,1), area 50.1mm2, adj f18,f24
  f24: cylinder r=5.4mm len=10.79mm, axis (0,0,1), area 17mm2, adj f23,f25
  f25: torus R=5.4mm, axis (0,0,1), area 50.1mm2, adj f19,f24
PLACE A t=(-4.96,-12.22,5.2)mm
PLACE B t=(-4.96,-12.22,4.2)mm
MATE revolute B.f0 <-> A.f1  axis (0,0,1) through (-4.96,-12.22,11.2)mm
